# Revit family: E-34_RFA
name_source: partatom
category: Aparatos sanitarios
units: mm (PartAtom-declared; Revit-internal decimal feet)

## family parameters
Compartido = No
Corte con vacíos al cargar = No
Cota de conector redondo = Diámetro de uso
Número OmniClass = 23.45.00.00
Punto de cálculo de habitación = No
Se basa en plano de trabajo = No
Siempre vertical = Sí
Tipo de pieza = Normal
Título OmniClass = Sanitary, Laundry, and Cleaning Equipment

## types (1)
- E-34
    Brass Chromed = Brass
    Certification = http://helvex.com
    Comentarios de tipo = Single Control Kitchen Faucet
    Data Sheet = http://helvex.com
    Descripción = Novus Single Control
    Elevación por defecto = 0"
    Fabricante = HELVEX
    Features = Includes Escutcheon Covers Drills; Ceramic Single Control Cartridge; Flexible Hoses 24" Long; Rotating Out; Installation Includes Key
    Inlet Threads = ½" - 14 NPSM
    Instructive = http://helvex.com
    Max. Working Pressure = 85.3 psi
    Min. Working Pressure = 8.5 psi
    Modelo = E-34
    Satin = Satín Duravex
    Total Height = 6"
    Total Length = 10"
    Total Width = 9"
    URL = http://helvex.com

## geometry (parser evidence)
native form markers: Sweep x3
no freeform markers — native parametric forms only
